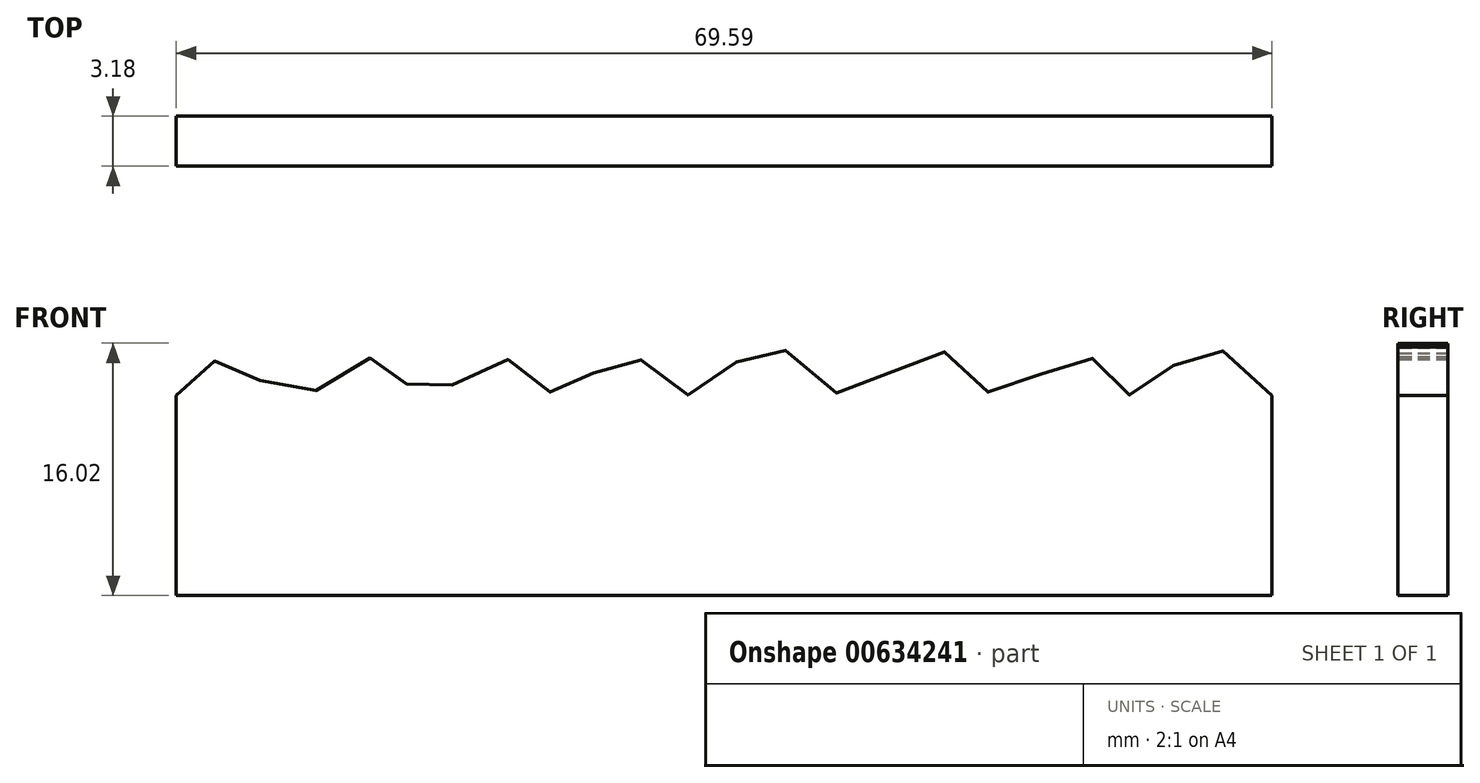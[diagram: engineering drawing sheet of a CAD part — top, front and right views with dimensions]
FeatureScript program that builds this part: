
annotation { "Feature Type Name" : "Feature", "Feature Type Description" : "" }
export const myFeature = defineFeature(function(context is Context, id is Id, definition is map)
    precondition{}
    {
        {
            var Q0;
            Q0=qCreatedBy(makeId("Front.planeOp"),FACE);
            var sketch = newSketch(context, id + "F0", { "sketchPlane" : qUnion([Q0])});
            skLineSegment(sketch, "E0", {"start": v(-37.52, 0) * mm, "end": v(-37.52, -12.7) * mm});
            skLineSegment(sketch, "E1", {"start": v(-37.52, -12.7) * mm, "end": v(32.07, -12.7) * mm});
            skLineSegment(sketch, "E2", {"start": v(32.07, -12.7) * mm, "end": v(32.07, 0) * mm});
            skFitSpline(sketch, "E3", {"points": [v(-37.52, 0) * mm, v(-34.48, 2.27) * mm, v(-29.75, 0) * mm, v(-24.61, 2.43) * mm, v(-21.82, 0) * mm, v(-16.58, 2.31) * mm, v(-13.12, 0) * mm, v(-9, 2.65) * mm, v(-4.75, 0) * mm, v(0, 3.32) * mm, v(5.07, 0) * mm, v(10.65, 2.98) * mm, v(14.67, 0) * mm, v(20.02, 2.65) * mm, v(23.15, 0) * mm, v(27.39, 2.98) * mm, v(32.07, 0) * mm], "startDerivative": vector(62.97, 57.06) * mm, "endDerivative": vector(71.53, -80.52) * mm});
            skSolve(sketch);
        }
        {
            var Q0;
            Q0 = qSketchRegion(id + "F0", true);
            extrude(context, id + "F1", {"entities" : qUnion([Q0]), "depth" : 3.17 * mm, "offsetDistance" : 25.4 * mm});
        }
    });
